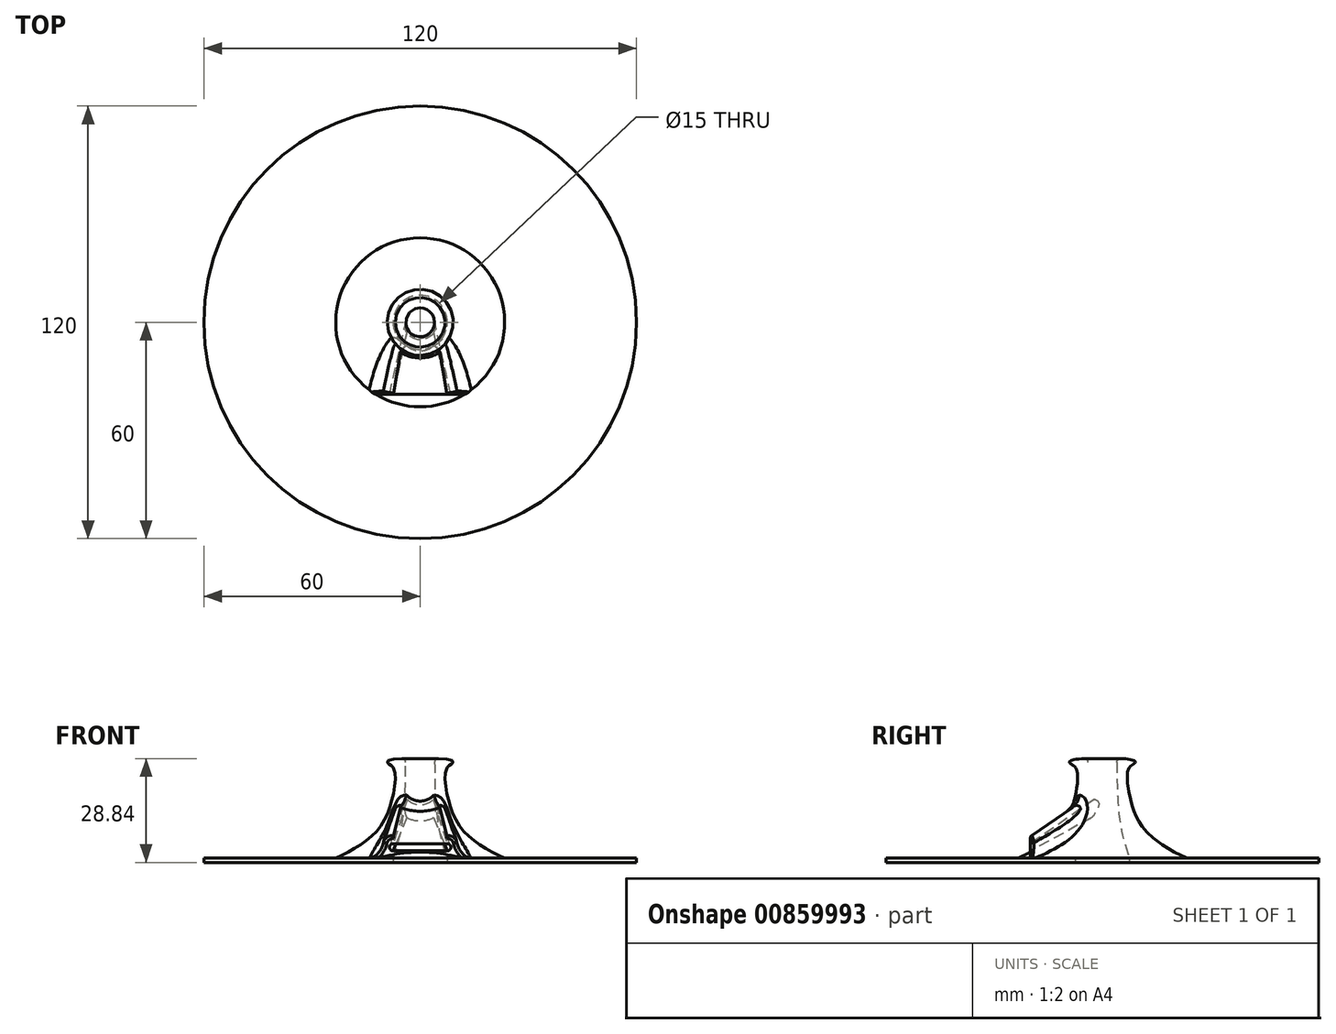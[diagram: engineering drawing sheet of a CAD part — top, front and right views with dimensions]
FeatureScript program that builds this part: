
annotation { "Feature Type Name" : "Feature", "Feature Type Description" : "" }
export const myFeature = defineFeature(function(context is Context, id is Id, definition is map)
    precondition{}
    {
        {
            var Q0;
            Q0=qCreatedBy(makeId("Top.planeOp"),FACE);
            var sketch = newSketch(context, id + "F0", { "sketchPlane" : qUnion([Q0])});
            skCircle(sketch, "E0", {"center": v(0, 0) * mm, "radius": 7.5 * mm});
            skCircle(sketch, "E1", {"center": v(0, 0) * mm, "radius": 60 * mm});
            skSolve(sketch);
        }
        {
            var Q0;
            Q0=makeQuery(id+"F0.imprint","IMPRINT",FACE,{"disambiguationData":[TD([[makeQuery(id+"F0.imprint","IMPRINT",EDGE,{"derivedFrom":sQuery(id+"F0.wireOp",EDGE,"E0")}),-1.0]])]});
            extrude(context, id + "F1", {"entities" : qUnion([Q0]), "depth" : 1.2 * mm, "offsetDistance" : 25 * mm});
        }
        {
            var Q0;
            Q0=qCreatedBy(makeId("Front.planeOp"),FACE);
            var sketch = newSketch(context, id + "F2", { "sketchPlane" : qUnion([Q0])});
            skLineSegment(sketch, "E2.0", {"start": v(-60, 1.2) * mm, "end": v(60, 1.2) * mm, "construction": true});
            skFitSpline(sketch, "E3", {"points": [v(-23.43, 1.2) * mm, v(-8.5, 15.03) * mm, v(-7.17, 25.83) * mm, v(-8.51, 27.18) * mm, v(0, 28.95) * mm], "startDerivative": vector(78.93, 35.86) * mm, "endDerivative": vector(130.58, 0) * mm});
            skLineSegment(sketch, "E4.0", {"start": v(-7.5, 1.2) * mm, "end": v(7.5, 1.2) * mm, "construction": true});
            skLineSegment(sketch, "E5", {"start": v(-23.43, 1.2) * mm, "end": v(-7.5, 1.2) * mm});
            skLineSegment(sketch, "E6", {"start": v(0, 28.95) * mm, "end": v(0, 1.2) * mm});
            skLineSegment(sketch, "E7", {"start": v(0, 1.2) * mm, "end": v(-23.43, 1.2) * mm});
            skSolve(sketch);
        }
        {
            var Q0;
            {var subQ0=sQuery(id+"F2.wireOp",EDGE,"E3");Q0=makeQuery(id+"F2.imprint","IMPRINT",FACE,{"disambiguationData":[TD([[makeQuery(id+"F2.imprint","IMPRINT",EDGE,{"derivedFrom":subQ0}),-1.0]])]});}
            var Q1;
            Q1=sQuery(id+"F2.wireOp",EDGE,"E6");
            revolve(context, id + "F3", {"surfaceOperationType" : NewSurfaceOperationType.NEW, "entities" : qUnion([Q0]), "axis" : qUnion([Q1]), "revolveType" : RevolveType.FULL});
        }
        {
            var Q0;
            Q0=qCreatedBy(makeId("Front.planeOp"),FACE);
            var sketch = newSketch(context, id + "F4", { "sketchPlane" : qUnion([Q0])});
            skArc(sketch, "E8", {"start": v(-3.12, 19.05) * mm, "mid": v(-4, 16.55) * mm, "end": v(-3.12, 14.05) * mm});
            skLineSegment(sketch, "E9.bottom", {"start": v(3.12, 14.05) * mm, "end": v(-3.12, 14.05) * mm});
            skLineSegment(sketch, "E9.top", {"start": v(3.12, 19.05) * mm, "end": v(-3.12, 19.05) * mm});
            skArc(sketch, "E10.trimOffspring", {"start": v(3.12, 14.05) * mm, "mid": v(4, 16.55) * mm, "end": v(3.12, 19.05) * mm});
            skSolve(sketch);
        }
        {
            var Q0;
            Q0=qCreatedBy(makeId("Front.planeOp"),FACE);
            var sketch = newSketch(context, id + "F5", { "sketchPlane" : qUnion([Q0])});
            skLineSegment(sketch, "E11.0", {"start": v(3.97, 21.05) * mm, "end": v(-3.97, 21.05) * mm});
            skArc(sketch, "E11.1", {"start": v(3.97, 12.05) * mm, "mid": v(6, 16.55) * mm, "end": v(3.97, 21.05) * mm});
            skLineSegment(sketch, "E11.2", {"start": v(3.97, 12.05) * mm, "end": v(-3.97, 12.05) * mm});
            skArc(sketch, "E11.3", {"start": v(-3.97, 21.05) * mm, "mid": v(-6, 16.55) * mm, "end": v(-3.97, 12.05) * mm});
            skSolve(sketch);
        }
        {
            var Q0;
            Q0=qCreatedBy(makeId("Front.planeOp"),FACE);
            cPlane(context, id + "F6", {"entities" : qUnion([Q0]), "cplaneType" : CPlaneType.OFFSET, "offset" : 20 * mm, "width" : 150 * mm, "height" : 150 * mm});
        }
        {
            var Q0;
            Q0=qCreatedBy(id+"F6.planeOp",FACE);
            var sketch = newSketch(context, id + "F7", { "sketchPlane" : qUnion([Q0])});
            skLineSegment(sketch, "E12.bottom", {"start": v(7.5, 3.2) * mm, "end": v(-7.5, 3.2) * mm});
            skLineSegment(sketch, "E12.top", {"start": v(7.5, 5.2) * mm, "end": v(-7.5, 5.2) * mm});
            skPoint(sketch, "E12.middle", {"position": v(0, 4.2) * mm});
            skArc(sketch, "E13", {"start": v(7.5, 3.2) * mm, "mid": v(8.5, 4.2) * mm, "end": v(7.5, 5.2) * mm});
            skArc(sketch, "E14.MirrorCS", {"start": v(-7.5, 3.2) * mm, "mid": v(-8.5, 4.2) * mm, "end": v(-7.5, 5.2) * mm});
            skSolve(sketch);
        }
        {
            var Q0;
            Q0=qCreatedBy(id+"F6.planeOp",FACE);
            var sketch = newSketch(context, id + "F8", { "sketchPlane" : qUnion([Q0])});
            skLineSegment(sketch, "E15.0", {"start": v(7.5, 7.2) * mm, "end": v(-7.5, 7.2) * mm});
            skArc(sketch, "E15.1", {"start": v(7.5, 1.2) * mm, "mid": v(10.5, 4.2) * mm, "end": v(7.5, 7.2) * mm});
            skLineSegment(sketch, "E15.2", {"start": v(7.5, 1.2) * mm, "end": v(-7.5, 1.2) * mm});
            skArc(sketch, "E15.3", {"start": v(-7.5, 1.2) * mm, "mid": v(-10.5, 4.2) * mm, "end": v(-7.5, 7.2) * mm});
            skSolve(sketch);
        }
        {
            var Q1;
            Q1 = qSketchRegion(id + "F5", true);
            var Q2;
            Q2 = qSketchRegion(id + "F8", true);
            loft(context, id + "F9", {"operationType" : NewBodyOperationType.ADD, "sheetProfilesArray" : [{ "sheetProfileEntities" : qUnion([Q1]) }, { "sheetProfileEntities" : qUnion([Q2]) }]});
        }
        {
            var Q1;
            Q1=makeQuery(id+"F4.imprint","IMPRINT",FACE,{"disambiguationData":[TD([[makeQuery(id+"F4.imprint","IMPRINT",EDGE,{"derivedFrom":sQuery(id+"F4.wireOp",EDGE,"E8")}),1.0]])]});
            var Q2;
            Q2=makeQuery(id+"F7.imprint","IMPRINT",FACE,{"disambiguationData":[TD([[makeQuery(id+"F7.imprint","IMPRINT",EDGE,{"derivedFrom":sQuery(id+"F7.wireOp",EDGE,"E12.bottom")}),-1.0]])]});
            loft(context, id + "F10", {"operationType" : NewBodyOperationType.REMOVE, "sheetProfilesArray" : [{ "sheetProfileEntities" : qUnion([Q1]) }, { "sheetProfileEntities" : qUnion([Q2]) }]});
        }
        {
            var Q0;
            Q0=qCreatedBy(makeId("Front.planeOp"),FACE);
            var sketch = newSketch(context, id + "F11", { "sketchPlane" : qUnion([Q0])});
            skPoint(sketch, "E16.0", {"position": v(-7.5, 1.2) * mm});
            skFitSpline(sketch, "E17.0", {"points": [v(-23.43, 1.2) * mm, v(-13.65, 5.64) * mm, v(-8.01, 12.35) * mm, v(-6.2, 26.02) * mm, v(-9.14, 27.38) * mm, v(-10.57, 28.95) * mm, v(0, 28.95) * mm], "construction": true});
            skFitSpline(sketch, "E18", {"points": [v(-7.5, 1.2) * mm, v(-4, 30.02) * mm], "startDerivative": vector(9.04, 25.18) * mm, "endDerivative": vector(0, 45.79) * mm});
            skLineSegment(sketch, "E19", {"start": v(-4, 30.02) * mm, "end": v(0, 30.02) * mm});
            skLineSegment(sketch, "E20", {"start": v(0, 30.02) * mm, "end": v(0, 1.2) * mm});
            skLineSegment(sketch, "E21", {"start": v(0, 1.2) * mm, "end": v(-7.5, 1.2) * mm});
            skSolve(sketch);
        }
        {
            var Q0;
            Q0 = qSketchRegion(id + "F11", true);
            var Q1;
            Q1=sQuery(id+"F11.wireOp",EDGE,"E20");
            revolve(context, id + "F12", {"operationType" : NewBodyOperationType.REMOVE, "surfaceOperationType" : NewSurfaceOperationType.NEW, "entities" : qUnion([Q0]), "axis" : qUnion([Q1]), "revolveType" : RevolveType.FULL, "oppositeDirection" : true});
        }
        {
            var Q0;
            Q0=makeQuery(id+"F9.boolean.opBoolean","INTERSECT",EDGE,{"derivedFrom":[makeQuery(id+"F3.opRevolve","SWEPT_FACE",FACE,{"disambiguationData":[OSD([sQuery(id+"F2.wireOp",EDGE,"E3")])]}),makeQuery(id+"F9.opLoft","SWEPT_FACE",FACE,{"disambiguationData":[OSD([sQuery(id+"F5.wireOp",EDGE,"E11.0"),sQuery(id+"F5.wireOp",EDGE,"E11.1"),sQuery(id+"F5.wireOp",EDGE,"E11.3"),sQuery(id+"F8.wireOp",EDGE,"E15.0"),sQuery(id+"F8.wireOp",EDGE,"E15.1"),sQuery(id+"F8.wireOp",EDGE,"E15.3")])]})]});
            var Q1;
            Q1=makeQuery(id+"F9.boolean.opBoolean","INTERSECT",EDGE,{"derivedFrom":[makeQuery(id+"F3.opRevolve","SWEPT_FACE",FACE,{"disambiguationData":[OSD([sQuery(id+"F2.wireOp",EDGE,"E3")])]}),makeQuery(id+"F9.opLoft","SWEPT_FACE",FACE,{"disambiguationData":[OSD([sQuery(id+"F5.wireOp",EDGE,"E11.0"),sQuery(id+"F5.wireOp",EDGE,"E11.2"),sQuery(id+"F5.wireOp",EDGE,"E11.3"),sQuery(id+"F8.wireOp",EDGE,"E15.0"),sQuery(id+"F8.wireOp",EDGE,"E15.2"),sQuery(id+"F8.wireOp",EDGE,"E15.3")])]})]});
            var Q2;
            Q2=makeQuery(id+"F9.boolean.opBoolean","INTERSECT",EDGE,{"derivedFrom":[makeQuery(id+"F3.opRevolve","SWEPT_FACE",FACE,{"disambiguationData":[OSD([sQuery(id+"F2.wireOp",EDGE,"E3")])]}),makeQuery(id+"F9.opLoft","SWEPT_FACE",FACE,{"disambiguationData":[OSD([sQuery(id+"F5.wireOp",EDGE,"E11.0"),sQuery(id+"F5.wireOp",EDGE,"E11.1"),sQuery(id+"F5.wireOp",EDGE,"E11.2"),sQuery(id+"F8.wireOp",EDGE,"E15.0"),sQuery(id+"F8.wireOp",EDGE,"E15.1"),sQuery(id+"F8.wireOp",EDGE,"E15.2")])]})]});
            fillet(context, id + "F13", {"entities" : qUnion([Q0, Q1, Q2]), "radius" : 5 * mm, "tangentPropagation" : true, "allowEdgeOverflow" : false});
        }
        {
            var Q0;
            Q0=makeQuery(id+"F9.opLoft","MID_CAP_EDGE",EDGE,{"disambiguationData":[OSD([sQuery(id+"F8.wireOp",EDGE,"E15.0"),sQuery(id+"F8.wireOp",EDGE,"E15.1"),sQuery(id+"F8.wireOp",EDGE,"E15.3")])],"capPos":1.0});
            var Q1;
            {var subQ0=sQuery(id+"F8.wireOp",EDGE,"E15.0");var subQ1=sQuery(id+"F8.wireOp",EDGE,"E15.1");var subQ2=sQuery(id+"F8.wireOp",EDGE,"E15.2");Q1=makeQuery(id+"F13.opFillet","BLEND_EDGE",EDGE,{"blendedFrom":[makeQuery(id+"F9.boolean.opBoolean","INTERSECT",EDGE,{"derivedFrom":[makeQuery(id+"F3.opRevolve","SWEPT_FACE",FACE,{"disambiguationData":[OSD([sQuery(id+"F2.wireOp",EDGE,"E3")])]}),makeQuery(id+"F9.opLoft","SWEPT_FACE",FACE,{"disambiguationData":[OSD([sQuery(id+"F5.wireOp",EDGE,"E11.0"),sQuery(id+"F5.wireOp",EDGE,"E11.1"),sQuery(id+"F5.wireOp",EDGE,"E11.2"),subQ0,subQ1,subQ2])]})]}),makeQuery(id+"F9.opLoft","CAP_FACE",FACE,{"disambiguationData":[OSD([makeQuery(id+"F8.imprint","IMPRINT",FACE,{"disambiguationData":[TD([[makeQuery(id+"F8.imprint","IMPRINT",EDGE,{"derivedFrom":subQ0}),1.0]])]})])],"isStart":true})],"blendedInto":[makeQuery(id+"F9.opLoft","CAP_FACE",FACE,{"disambiguationData":[OSD([makeQuery(id+"F8.imprint","IMPRINT",FACE,{"disambiguationData":[TD([[makeQuery(id+"F8.imprint","IMPRINT",EDGE,{"derivedFrom":subQ0}),1.0]])]})])],"isStart":true})]});}
            var Q2;
            Q2=makeQuery(id+"F9.opLoft","MID_CAP_EDGE",EDGE,{"disambiguationData":[OSD([sQuery(id+"F8.wireOp",EDGE,"E15.0"),sQuery(id+"F8.wireOp",EDGE,"E15.1"),sQuery(id+"F8.wireOp",EDGE,"E15.2")])],"capPos":1.0});
            var Q3;
            Q3=makeQuery(id+"F9.opLoft","MID_CAP_EDGE",EDGE,{"disambiguationData":[OSD([sQuery(id+"F8.wireOp",EDGE,"E15.0"),sQuery(id+"F8.wireOp",EDGE,"E15.2"),sQuery(id+"F8.wireOp",EDGE,"E15.3")])],"capPos":1.0});
            var Q4;
            {var subQ0=sQuery(id+"F8.wireOp",EDGE,"E15.0");var subQ1=sQuery(id+"F8.wireOp",EDGE,"E15.2");var subQ2=sQuery(id+"F8.wireOp",EDGE,"E15.3");Q4=makeQuery(id+"F13.opFillet","BLEND_EDGE",EDGE,{"blendedFrom":[makeQuery(id+"F9.boolean.opBoolean","INTERSECT",EDGE,{"derivedFrom":[makeQuery(id+"F3.opRevolve","SWEPT_FACE",FACE,{"disambiguationData":[OSD([sQuery(id+"F2.wireOp",EDGE,"E3")])]}),makeQuery(id+"F9.opLoft","SWEPT_FACE",FACE,{"disambiguationData":[OSD([sQuery(id+"F5.wireOp",EDGE,"E11.0"),sQuery(id+"F5.wireOp",EDGE,"E11.2"),sQuery(id+"F5.wireOp",EDGE,"E11.3"),subQ0,subQ1,subQ2])]})]}),makeQuery(id+"F9.opLoft","CAP_FACE",FACE,{"disambiguationData":[OSD([makeQuery(id+"F8.imprint","IMPRINT",FACE,{"disambiguationData":[TD([[makeQuery(id+"F8.imprint","IMPRINT",EDGE,{"derivedFrom":subQ0}),1.0]])]})])],"isStart":true})],"blendedInto":[makeQuery(id+"F9.opLoft","CAP_FACE",FACE,{"disambiguationData":[OSD([makeQuery(id+"F8.imprint","IMPRINT",FACE,{"disambiguationData":[TD([[makeQuery(id+"F8.imprint","IMPRINT",EDGE,{"derivedFrom":subQ0}),1.0]])]})])],"isStart":true})]});}
            var Q5;
            Q5=makeQuery(id+"F12.boolean.opBoolean","INTERSECT",EDGE,{"derivedFrom":[makeQuery(id+"F3.opRevolve","SWEPT_FACE",FACE,{"disambiguationData":[OSD([sQuery(id+"F2.wireOp",EDGE,"E3")])]}),makeQuery(id+"F12.opRevolve","SWEPT_FACE",FACE,{"disambiguationData":[OSD([sQuery(id+"F11.wireOp",EDGE,"E18")])]})]});
            fillet(context, id + "F14", {"entities" : qUnion([Q0, Q1, Q2, Q3, Q4, Q5]), "radius" : 1 * mm, "tangentPropagation" : true, "allowEdgeOverflow" : false});
        }
    });
